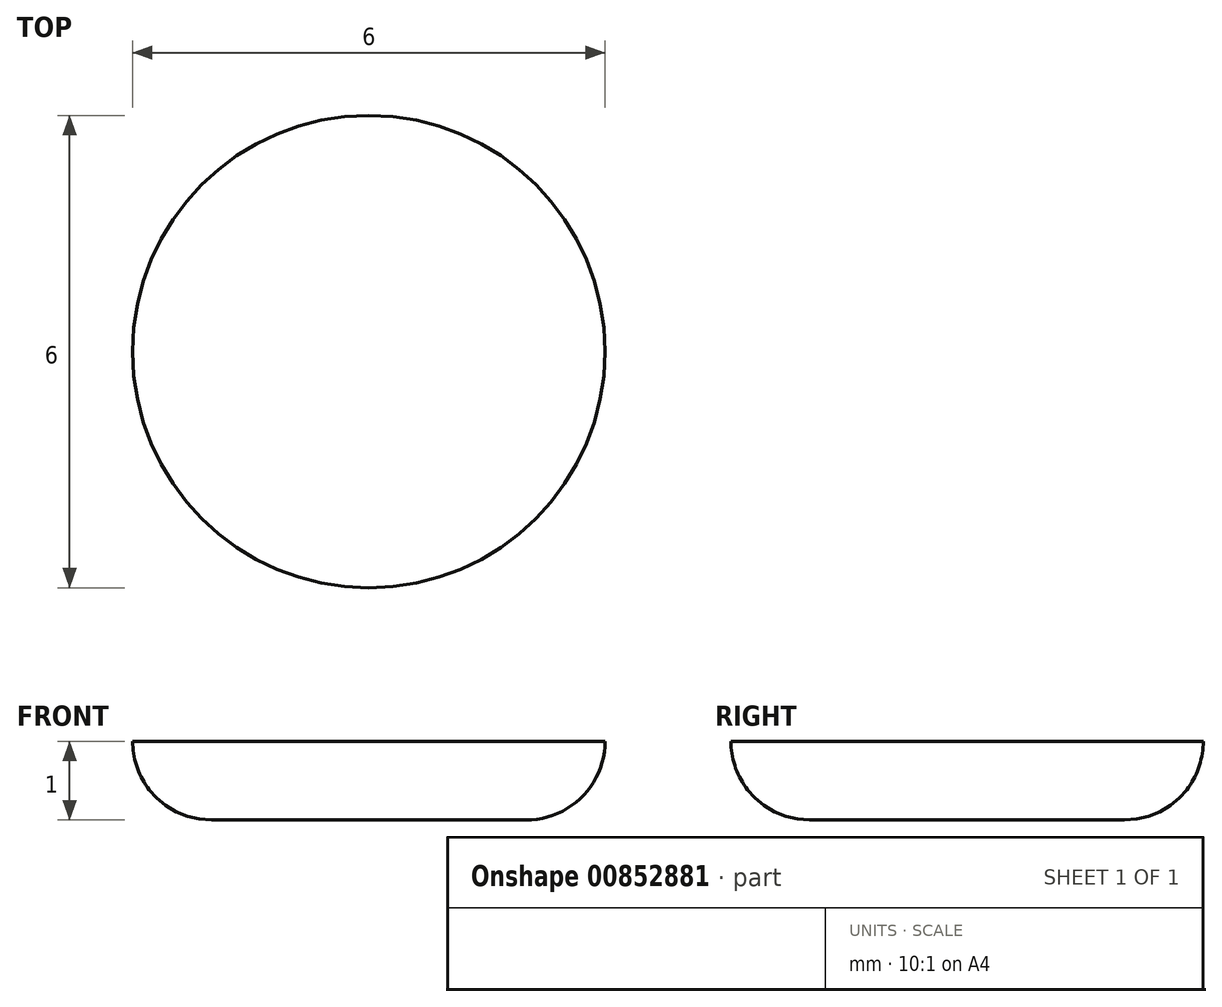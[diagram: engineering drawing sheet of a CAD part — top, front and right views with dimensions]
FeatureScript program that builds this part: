
annotation { "Feature Type Name" : "Feature", "Feature Type Description" : "" }
export const myFeature = defineFeature(function(context is Context, id is Id, definition is map)
    precondition{}
    {
        {
            var Q0;
            Q0=qCreatedBy(makeId("Top.planeOp"),FACE);
            var sketch = newSketch(context, id + "F0", { "sketchPlane" : qUnion([Q0])});
            skCircle(sketch, "E0", {"center": v(0, 0) * mm, "radius": 3 * mm});
            skSolve(sketch);
        }
        {
            var Q0;
            Q0=makeQuery(id+"F0.imprint","IMPRINT",FACE,{"disambiguationData":[TD([[makeQuery(id+"F0.imprint","IMPRINT",EDGE,{"derivedFrom":sQuery(id+"F0.wireOp",EDGE,"E0")}),1.0]])]});
            extrude(context, id + "F1", {"entities" : qUnion([Q0]), "depth" : 1 * mm, "offsetDistance" : 25 * mm});
        }
        {
            var Q0;
            Q0=makeQuery(id+"FC5OAHJJxmZf4sP_1.opExtrude","CAP_EDGE",EDGE,{"disambiguationData":[OSD([sQuery(id+"F0.wireOp",EDGE,"E0")])],"isStart":false});
            var Q1;
            Q1=makeQuery(id+"F1.opExtrude","CAP_EDGE",EDGE,{"disambiguationData":[OSD([sQuery(id+"F0.wireOp",EDGE,"E0")])],"isStart":true});
            fillet(context, id + "F2", {"entities" : qUnion([Q0, Q1]), "radius" : 1 * mm, "tangentPropagation" : true, "allowEdgeOverflow" : false});
        }
    });
